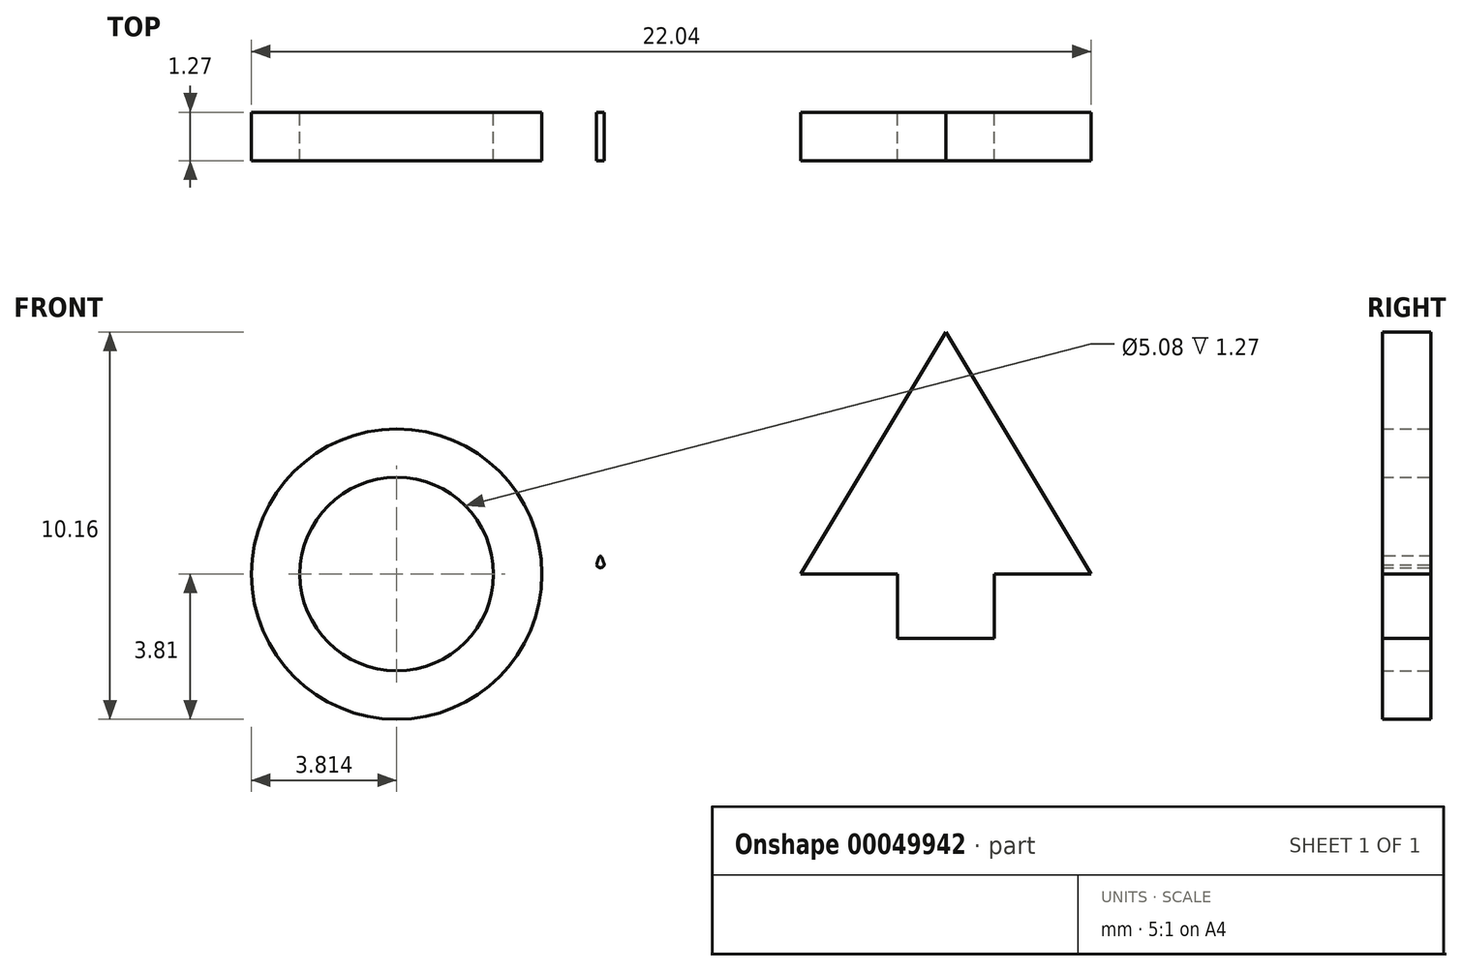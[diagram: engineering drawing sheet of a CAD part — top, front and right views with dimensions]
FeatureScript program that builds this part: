
annotation { "Feature Type Name" : "Feature", "Feature Type Description" : "" }
export const myFeature = defineFeature(function(context is Context, id is Id, definition is map)
    precondition{}
    {
        {
            var Q0;
            Q0=qCreatedBy(makeId("Front.planeOp"),FACE);
            var sketch = newSketch(context, id + "F0", { "sketchPlane" : qUnion([Q0])});
            skLineSegment(sketch, "E0", {"start": v(0, 0) * mm, "end": v(7.62, 0) * mm});
            skLineSegment(sketch, "E1", {"start": v(3.8, 0) * mm, "end": v(3.8, 6.35) * mm});
            skLineSegment(sketch, "E2", {"start": v(3.8, 6.35) * mm, "end": v(7.62, 0) * mm});
            skLineSegment(sketch, "E3", {"start": v(3.81, 6.35) * mm, "end": v(0, 0) * mm});
            skLineSegment(sketch, "E4", {"start": v(3.8, 0) * mm, "end": v(5.08, 0) * mm});
            skLineSegment(sketch, "E5", {"start": v(3.8, 0) * mm, "end": v(2.54, 0) * mm});
            skLineSegment(sketch, "E6", {"start": v(2.54, 0) * mm, "end": v(2.54, -1.69) * mm});
            skLineSegment(sketch, "E7", {"start": v(2.54, -1.69) * mm, "end": v(5.08, -1.69) * mm});
            skLineSegment(sketch, "E8", {"start": v(5.08, 0) * mm, "end": v(5.08, -1.69) * mm});
            skLineSegment(sketch, "E9", {"start": v(0, 0) * mm, "end": v(0.13, 0.22) * mm});
            skLineSegment(sketch, "E10", {"start": v(0, 0) * mm, "end": v(0.25, 0) * mm});
            skArc(sketch, "E11", {"start": v(0.13, 0.22) * mm, "mid": v(0.13, 0.07) * mm, "end": v(0.25, 0) * mm});
            skLineSegment(sketch, "E12", {"start": v(7.62, 0) * mm, "end": v(7.49, 0.22) * mm});
            skLineSegment(sketch, "E13", {"start": v(7.62, 0) * mm, "end": v(7.37, 0) * mm});
            skArc(sketch, "E14", {"start": v(7.37, 0) * mm, "mid": v(7.5, 0.07) * mm, "end": v(7.49, 0.22) * mm});
            skCircle(sketch, "E15", {"center": v(-10.6, 0) * mm, "radius": 2.54 * mm});
            skCircle(sketch, "E16", {"center": v(-10.6, 0) * mm, "radius": 3.8 * mm});
            skLineSegment(sketch, "E17", {"start": v(-10.6, 0) * mm, "end": v(-8.07, 0) * mm});
            skLineSegment(sketch, "E18", {"start": v(-10.6, 0) * mm, "end": v(-14.42, 0) * mm});
            skLineSegment(sketch, "E19", {"start": v(-5.36, 0.24) * mm, "end": v(-5.16, 0.24) * mm});
            skLineSegment(sketch, "E20", {"start": v(-5.26, 0.24) * mm, "end": v(-5.26, 0.17) * mm});
            skArc(sketch, "E21", {"start": v(-5.36, 0.24) * mm, "mid": v(-5.26, 0.17) * mm, "end": v(-5.16, 0.24) * mm});
            skLineSegment(sketch, "E22", {"start": v(-5.26, 0.17) * mm, "end": v(-5.26, 0.47) * mm});
            skFitSpline(sketch, "E23", {"points": [v(-5.16, 0.24) * mm, v(-5.16, 0.24) * mm], "startDerivative": vector(0, 0) * mm, "endDerivative": vector(0, 0) * mm});
            skFitSpline(sketch, "E24", {"points": [v(-5.36, 0.24) * mm, v(-5.26, 0.47) * mm, v(-5.16, 0.24) * mm], "startDerivative": vector(0.2, 0.69) * mm, "endDerivative": vector(0.2, -0.69) * mm});
            skSolve(sketch);
        }
        {
            var Q0;
            Q0 = qSketchRegion(id + "F0", true);
            extrude(context, id + "F1", {"entities" : qUnion([Q0]), "depth" : 1.27 * mm});
        }
    });
